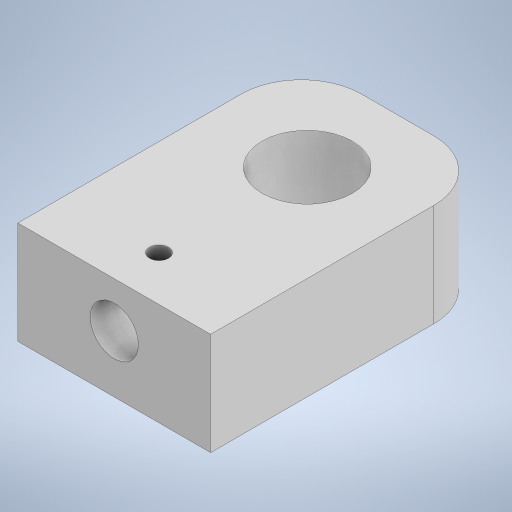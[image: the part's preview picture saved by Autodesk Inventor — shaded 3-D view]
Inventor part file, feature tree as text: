
AUTODESK INVENTOR PART (.ipt)
format: ipt  version: 2023 (Build 270158000, 158)  size: 451,072 bytes
history: native  units: mm
features: sketch x13, extrude x10, hole x3, fillet x1, projected_geometry x1
ambient origin geometry x8: Origin, YZ Plane, XZ Plane, XY Plane, X Axis, Y Axis, Z Axis, Center Point
bodies: Solid1 (feature_tree)
feature tree (28):
  extrude  "Extrusion1"  Depth=24.2mm TaperAngle=0.0deg
  extrude  "Extrusion3"  Depth=2.0mm
  extrude  "Extrusion4"  Depth=3.0mm TaperAngle=0.0deg
  extrude  "Extrusion5"  Depth=130.0mm TaperAngle=0.0deg
  hole  "Hole1"  [1 undecoded]
  hole  "Hole3"  [1 undecoded]
  extrude  "Extrusion6"  Depth=10.0mm
  extrude  "Extrusion7"  Depth=10.0mm
  fillet  "Fillet1"  Radius=4.0mm
  hole  "Hole4"  [1 undecoded]
  extrude  "Extrusion8"  Depth=10.0mm
  extrude  "Extrusion9"  Depth=10.0mm
  extrude  "Extrusion10"  Depth=10.0mm
  extrude  "Extrusion11"  Depth=10.0mm
  sketch  "Sketch1"  dims[d0=15.0mm d3=24.2mm d4=0.0mm]
  sketch  "Sketch2"  dims[d5=32.0mm d6=2.0mm]
  projected_geometry  "Projected Loop1"
  sketch  "Sketch4"  dims[d10=8.5mm d11=3.0mm d12=0.0mm]
  sketch  "Sketch5"  dims[d13=3.0mm d14=0.0mm d15=130.0mm d16=0.0mm]
  sketch  "Sketch6"  dims[d17=3.5mm d18=3.5mm]
  sketch  "Sketch7"  dims[d19=2.38125mm d20=6.0mm d21=4.0mm d22=2.0mm d23=90.0deg d24=10.0mm d25=20.594885mm d27=3.5mm]
  sketch  "Sketch8"  dims[d42=50.0mm d44=30.0mm d45=10.0mm d47=10.0mm d49=3.5mm]
  sketch  "Sketch9"  dims[d50=15.0mm]
  sketch  "Sketch10"  dims[d51=3.175mm d52=6.0mm d53=4.0mm d54=2.0mm d55=90.0deg d56=10.0mm d57=20.594885mm d58=6.0mm]
  sketch  "Sketch11"  dims[d59=20.0mm d61=25.0mm d62=10.0mm d64=10.0mm]
  sketch  "Sketch12"  dims[d66=50.0mm d68=30.0mm d69=10.0mm d71=10.0mm]
  sketch  "Sketch13"  dims[d73=50.0mm d75=30.0mm d76=10.0mm d78=10.0mm]
  sketch  "Sketch14"  dims[d80=20.0mm d82=21.5mm d83=10.0mm d85=10.0mm d87=4.0mm d88=0.0mm d89=50.0mm d90=0.0mm d91=10.0mm d94=15.0mm d95=15.0mm d96=6.0mm d97=4.0mm d98=2.0mm d99=90.0deg d100=8.0mm d101=20.594885mm d102=25.0mm d103=3.0mm d104=15.0mm d105=0.0mm d106=163.2mm d107=0.0mm d108=8.0mm d109=10.0mm d110=0.0mm d111=3.175mm d112=10.0mm d113=0.0mm]
note: 3 required parameter values undecoded (feature->parameter linkage not recoverable at this tier; creation-order binding heuristic only, values carry confidence <= 0.55)
